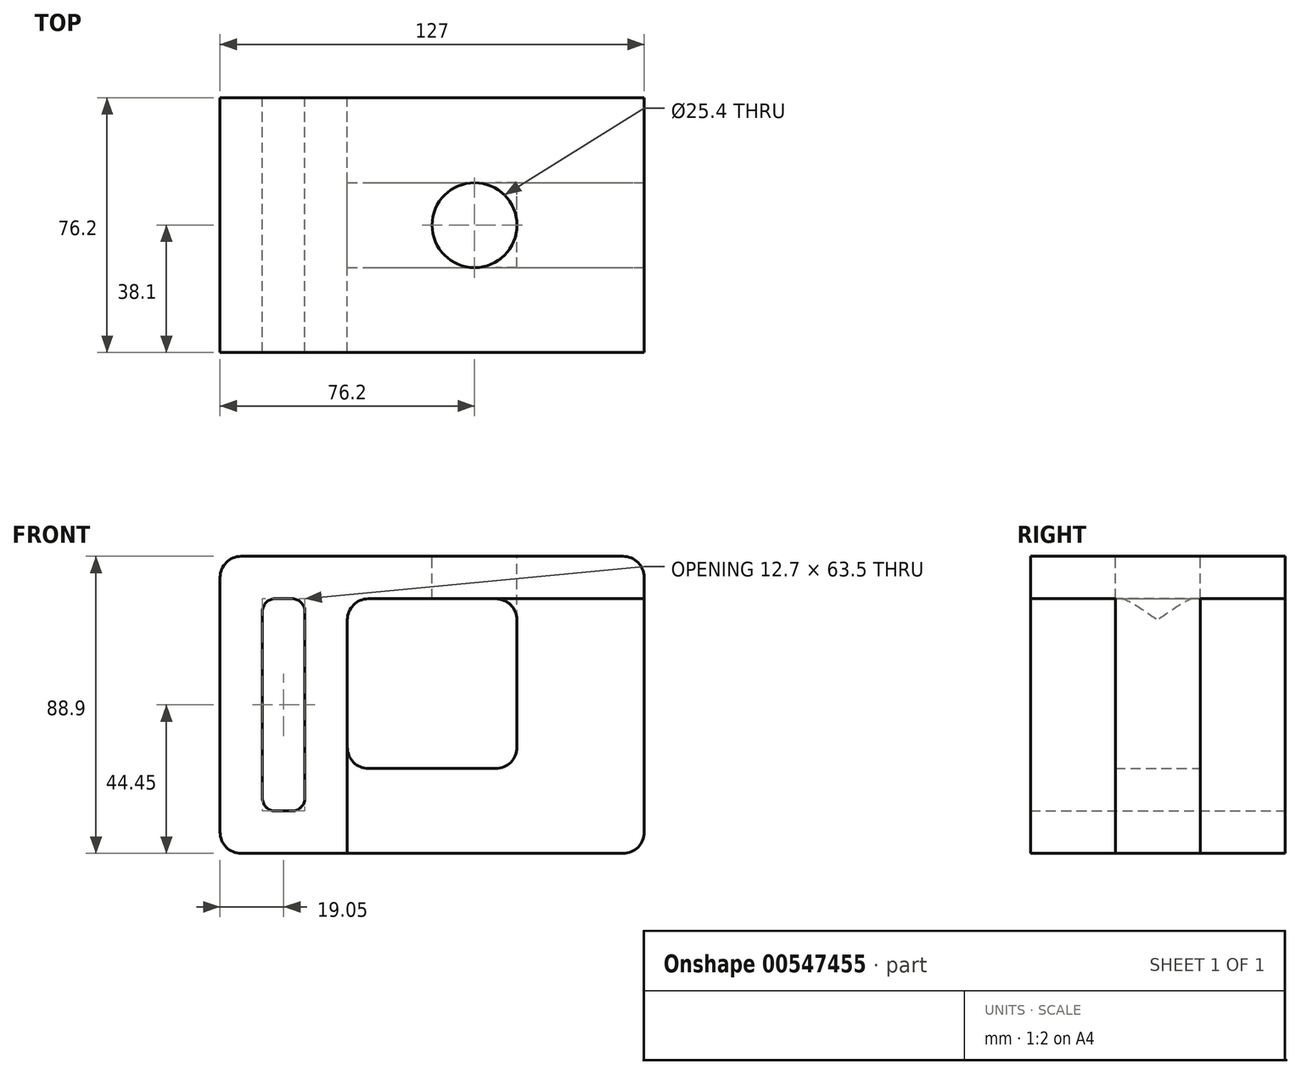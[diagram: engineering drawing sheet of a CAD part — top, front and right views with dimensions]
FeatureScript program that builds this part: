
annotation { "Feature Type Name" : "Feature", "Feature Type Description" : "" }
export const myFeature = defineFeature(function(context is Context, id is Id, definition is map)
    precondition{}
    {
        {
            var Q0;
            Q0=qCreatedBy(makeId("Front.planeOp"),FACE);
            var sketch = newSketch(context, id + "F0", { "sketchPlane" : qUnion([Q0])});
            skLineSegment(sketch, "E0.bottom", {"start": v(6.35, 0) * mm, "end": v(44.45, 0) * mm});
            skLineSegment(sketch, "E0.top", {"start": v(6.35, -50.8) * mm, "end": v(44.45, -50.8) * mm});
            skLineSegment(sketch, "E0.left", {"start": v(0, -6.35) * mm, "end": v(0, -44.45) * mm});
            skLineSegment(sketch, "E0.right", {"start": v(50.8, -6.35) * mm, "end": v(50.8, -44.45) * mm});
            skLineSegment(sketch, "E1.bottom", {"start": v(-31.75, 12.7) * mm, "end": v(82.55, 12.7) * mm});
            skLineSegment(sketch, "E1.top", {"start": v(-31.75, -76.2) * mm, "end": v(82.55, -76.2) * mm});
            skLineSegment(sketch, "E1.left", {"start": v(-38.1, 6.35) * mm, "end": v(-38.1, -69.85) * mm});
            skLineSegment(sketch, "E1.right", {"start": v(88.9, 6.35) * mm, "end": v(88.9, -69.85) * mm});
            skLineSegment(sketch, "E2.bottom", {"start": v(-21.59, 0) * mm, "end": v(-16.51, 0) * mm});
            skLineSegment(sketch, "E2.top", {"start": v(-21.59, -63.5) * mm, "end": v(-16.5, -63.5) * mm});
            skLineSegment(sketch, "E2.left", {"start": v(-25.4, -3.8) * mm, "end": v(-25.4, -59.69) * mm});
            skLineSegment(sketch, "E2.right", {"start": v(-12.7, -3.8) * mm, "end": v(-12.7, -59.69) * mm});
            skPoint(sketch, "E3.visualSharp", {"position": v(0, 0) * mm});
            skArc(sketch, "E3.filletArc", {"start": v(6.35, 0) * mm, "mid": v(1.86, -1.86) * mm, "end": v(0, -6.35) * mm});
            skPoint(sketch, "E4.visualSharp", {"position": v(50.8, 0) * mm});
            skArc(sketch, "E4.filletArc", {"start": v(50.8, -6.35) * mm, "mid": v(48.94, -1.86) * mm, "end": v(44.45, 0) * mm});
            skPoint(sketch, "E5.visualSharp", {"position": v(50.8, -50.8) * mm});
            skArc(sketch, "E5.filletArc", {"start": v(44.45, -50.8) * mm, "mid": v(48.94, -48.94) * mm, "end": v(50.8, -44.45) * mm});
            skPoint(sketch, "E6.visualSharp", {"position": v(0, -50.8) * mm});
            skArc(sketch, "E6.filletArc", {"start": v(0, -44.45) * mm, "mid": v(1.86, -48.94) * mm, "end": v(6.35, -50.8) * mm});
            skPoint(sketch, "E7.visualSharp", {"position": v(-12.7, -63.5) * mm});
            skArc(sketch, "E7.filletArc", {"start": v(-16.5, -63.5) * mm, "mid": v(-13.82, -62.38) * mm, "end": v(-12.7, -59.69) * mm});
            skPoint(sketch, "E8.visualSharp", {"position": v(-25.4, -63.5) * mm});
            skArc(sketch, "E8.filletArc", {"start": v(-25.4, -59.69) * mm, "mid": v(-24.28, -62.38) * mm, "end": v(-21.59, -63.5) * mm});
            skPoint(sketch, "E9.visualSharp", {"position": v(-25.4, 0) * mm});
            skArc(sketch, "E9.filletArc", {"start": v(-21.59, 0) * mm, "mid": v(-24.28, -1.12) * mm, "end": v(-25.4, -3.8) * mm});
            skPoint(sketch, "E10.visualSharp", {"position": v(-12.7, 0) * mm});
            skArc(sketch, "E10.filletArc", {"start": v(-12.7, -3.8) * mm, "mid": v(-13.82, -1.12) * mm, "end": v(-16.51, 0) * mm});
            skPoint(sketch, "E11.visualSharp", {"position": v(-38.1, 12.7) * mm});
            skArc(sketch, "E11.filletArc", {"start": v(-31.75, 12.7) * mm, "mid": v(-36.24, 10.84) * mm, "end": v(-38.1, 6.35) * mm});
            skPoint(sketch, "E12.visualSharp", {"position": v(88.9, 12.7) * mm});
            skArc(sketch, "E12.filletArc", {"start": v(88.9, 6.35) * mm, "mid": v(87.04, 10.84) * mm, "end": v(82.55, 12.7) * mm});
            skPoint(sketch, "E13.visualSharp", {"position": v(88.9, -76.2) * mm});
            skArc(sketch, "E13.filletArc", {"start": v(82.55, -76.2) * mm, "mid": v(87.04, -74.34) * mm, "end": v(88.9, -69.85) * mm});
            skPoint(sketch, "E14.visualSharp", {"position": v(-38.1, -76.2) * mm});
            skArc(sketch, "E14.filletArc", {"start": v(-38.1, -69.85) * mm, "mid": v(-36.24, -74.34) * mm, "end": v(-31.75, -76.2) * mm});
            skLineSegment(sketch, "E15", {"start": v(6.35, 0) * mm, "end": v(88.9, 0) * mm});
            skLineSegment(sketch, "E16", {"start": v(0, -6.35) * mm, "end": v(0, -76.2) * mm});
            skPoint(sketch, "E16.endSnap0", {"position": v(0, -25.4) * mm});
            skSolve(sketch);
        }
        {
            var Q0;
            Q0=makeQuery(id+"F0.imprint","IMPRINT",FACE,{"disambiguationData":[TD([[makeQuery(id+"F0.imprint","IMPRINT",EDGE,{"derivedFrom":sQuery(id+"F0.wireOp",EDGE,"E1.bottom")}),-1.0]])]});
            extrude(context, id + "F1", {"entities" : qUnion([Q0]), "endBound" : BoundingType.SYMMETRIC, "depth" : 76.2 * mm, "offsetDistance" : 25.4 * mm});
        }
        {
            var Q0;
            Q0 = qSketchRegion(id + "F0", true);
            extrude(context, id + "F2", {"entities" : qUnion([Q0]), "operationType" : NewBodyOperationType.ADD, "endBound" : BoundingType.SYMMETRIC, "depth" : 25.4 * mm, "offsetDistance" : 25.4 * mm});
        }
        {
            var Q0;
            Q0=makeQuery(id+"F1.opExtrude","SWEPT_FACE",FACE,{"disambiguationData":[OSD([sQuery(id+"F0.wireOp",EDGE,"E1.bottom")])]});
            var sketch = newSketch(context, id + "F3", { "sketchPlane" : qUnion([Q0])});
            skCircle(sketch, "E17", {"center": v(38.1, 0) * mm, "radius": 12.7 * mm});
            skSolve(sketch);
        }
        {
            var Q0;
            Q0=makeQuery(id+"F3.imprint","IMPRINT",FACE,{"disambiguationData":[TD([[makeQuery(id+"F3.imprint","IMPRINT",EDGE,{"derivedFrom":sQuery(id+"F3.wireOp",EDGE,"E17")}),1.0]])]});
            extrude(context, id + "F4", {"entities" : qUnion([Q0]), "operationType" : NewBodyOperationType.REMOVE, "oppositeDirection" : true, "depth" : 25.4 * mm, "offsetDistance" : 25.4 * mm});
        }
    });
